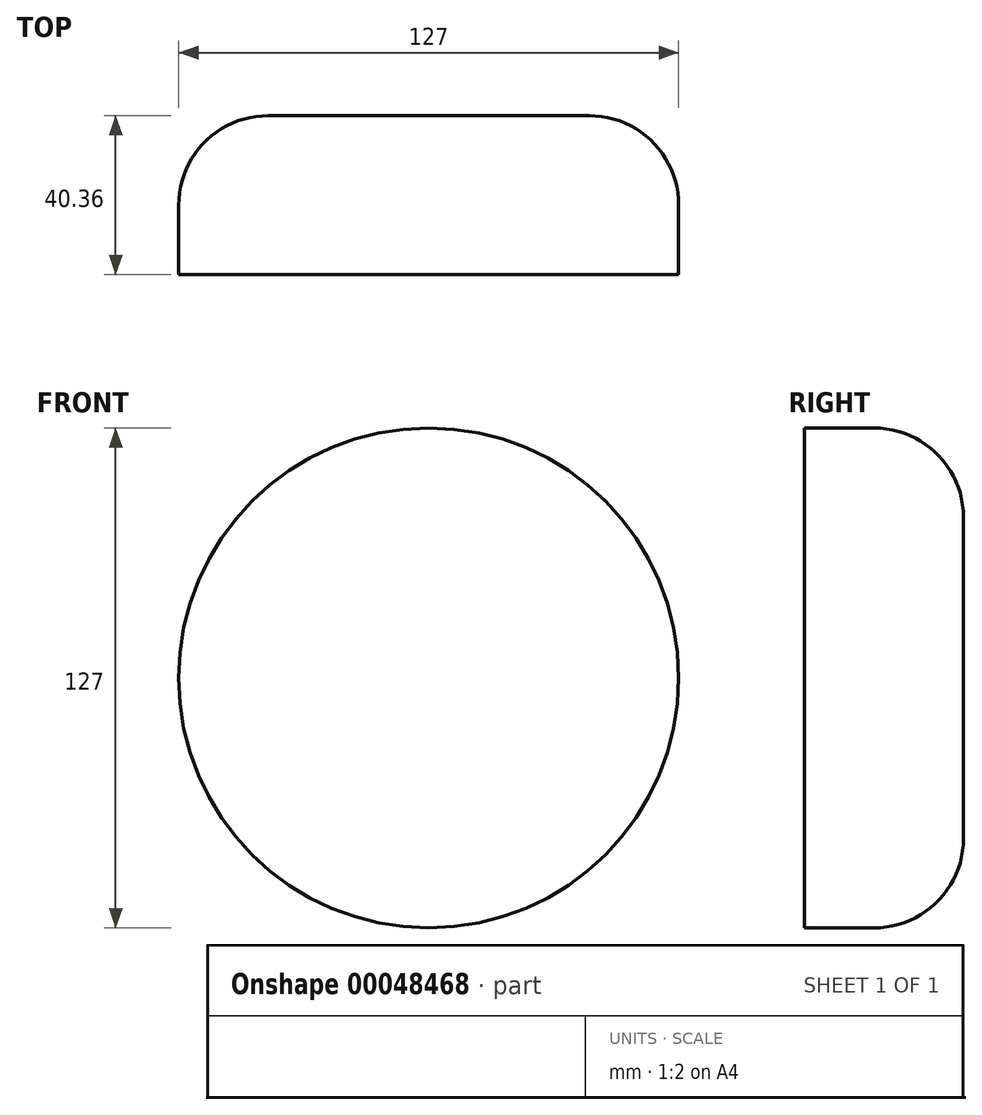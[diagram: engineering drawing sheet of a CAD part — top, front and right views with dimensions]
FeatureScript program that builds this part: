
annotation { "Feature Type Name" : "Feature", "Feature Type Description" : "" }
export const myFeature = defineFeature(function(context is Context, id is Id, definition is map)
    precondition{}
    {
        {
            var Q0;
            Q0=qCreatedBy(makeId("Front.planeOp"),FACE);
            var sketch = newSketch(context, id + "F0", { "sketchPlane" : qUnion([Q0])});
            skCircle(sketch, "E0", {"center": v(0, 0) * mm, "radius": 63.5 * mm});
            skSolve(sketch);
        }
        {
            var Q0;
            Q0 = qSketchRegion(id + "F0", true);
            extrude(context, id + "F1", {"entities" : qUnion([Q0]), "depth" : 40.36 * mm});
        }
        {
            var Q0;
            Q0=makeQuery(id+"F1.opExtrude","CAP_EDGE",EDGE,{"disambiguationData":[OSD([sQuery(id+"F0.wireOp",EDGE,"E0")])],"isStart":true});
            fillet(context, id + "F2", {"entities" : qUnion([Q0]), "radius" : 22.7 * mm, "tangentPropagation" : true, "allowEdgeOverflow" : false});
        }
    });
